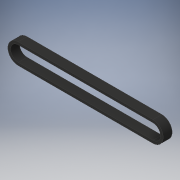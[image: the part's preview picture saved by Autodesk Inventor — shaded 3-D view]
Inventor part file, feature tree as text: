
AUTODESK INVENTOR PART (.ipt)
format: ipt  version: 2019 (Build 230136000, 136)  size: 108,544 bytes
history: native  units: mm
features: extrude x1, sketch x1
ambient origin geometry x8: Origin, YZ Plane, XZ Plane, XY Plane, X Axis, Y Axis, Z Axis, Center Point
bodies: Solid1 (feature_tree)
feature tree (2):
  extrude  "Extrusion1"  Depth=23.0mm
  sketch  "Sketch1"  dims[d0=151.0mm d1=23.0mm d2=3.0mm d3=3.0mm d4=11.5mm d5=8.5mm d7=8.5mm d8=151.0mm d9=151.0mm d10=10.0mm d11=0.0mm]
